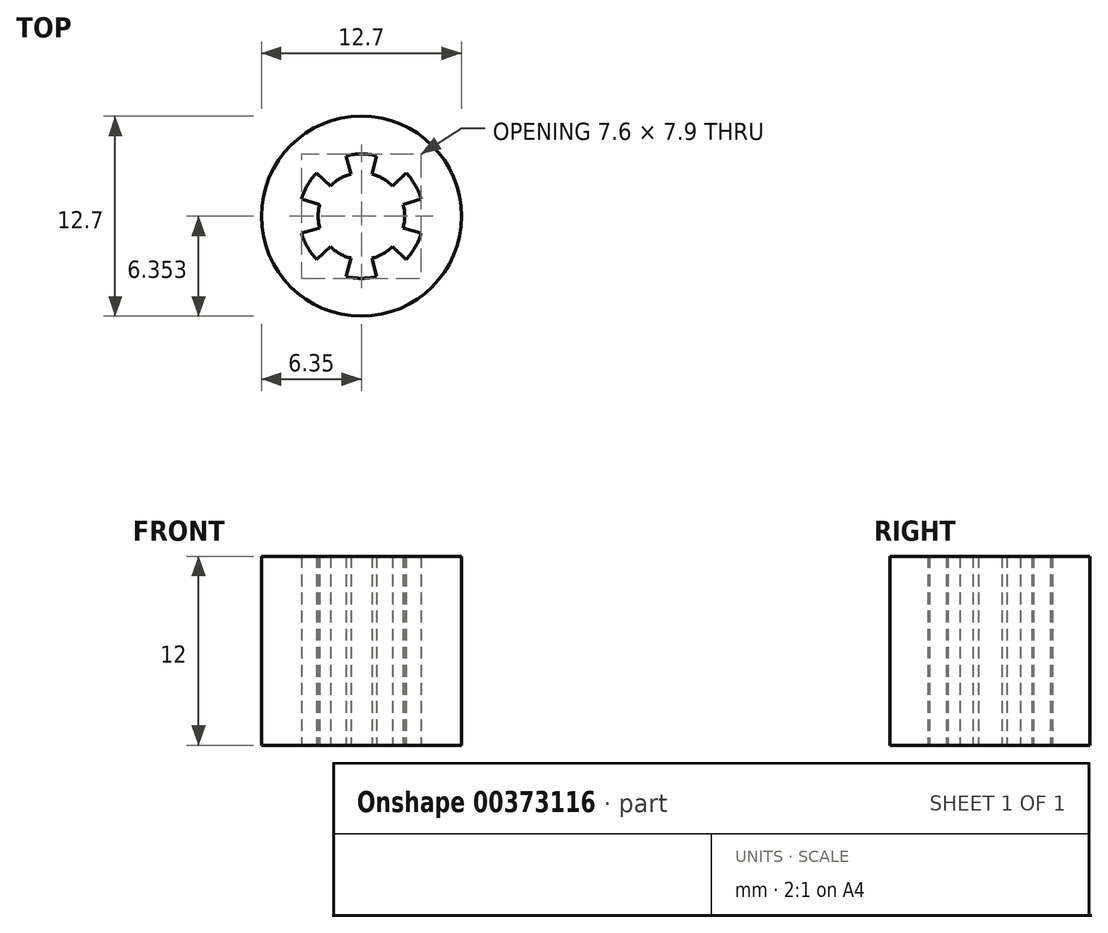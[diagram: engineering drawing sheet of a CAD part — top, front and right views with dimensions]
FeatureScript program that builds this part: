
annotation { "Feature Type Name" : "Feature", "Feature Type Description" : "" }
export const myFeature = defineFeature(function(context is Context, id is Id, definition is map)
    precondition{}
    {
        {
            var Q0;
            Q0=qCreatedBy(makeId("Top.planeOp"),FACE);
            var sketch = newSketch(context, id + "F0", { "sketchPlane" : qUnion([Q0])});
            skCircle(sketch, "E0.0", {"center": v(0, 0.1) * mm, "radius": 6.35 * mm});
            skArc(sketch, "E1", {"start": v(-2.65, 0.85) * mm, "mid": v(-2.75, 0.1) * mm, "end": v(-2.65, -0.65) * mm});
            skArc(sketch, "E2.0", {"start": v(-2.83, 2.86) * mm, "mid": v(-3.42, 2.08) * mm, "end": v(-3.8, 1.18) * mm});
            skLineSegment(sketch, "E3", {"start": v(0, 0.1) * mm, "end": v(0, 6.45) * mm, "construction": true});
            skLineSegment(sketch, "E4", {"start": v(-0.67, 2.77) * mm, "end": v(-0.97, 3.93) * mm});
            skLineSegment(sketch, "E5", {"start": v(-0.67, 2.77) * mm, "end": v(-2.33, 2.35) * mm, "construction": true});
            skLineSegment(sketch, "E6.MirrorCS", {"start": v(0.67, 2.77) * mm, "end": v(0.97, 3.93) * mm});
            skLineSegment(sketch, "E7.1.0", {"start": v(-1.97, 2.02) * mm, "end": v(-2.83, 2.86) * mm});
            skLineSegment(sketch, "E7.1.1", {"start": v(-2.65, 0.85) * mm, "end": v(-3.8, 1.18) * mm});
            skLineSegment(sketch, "E7.2.0", {"start": v(-2.65, -0.65) * mm, "end": v(-3.8, -0.97) * mm});
            skLineSegment(sketch, "E7.2.1", {"start": v(-1.97, -1.81) * mm, "end": v(-2.83, -2.65) * mm});
            skLineSegment(sketch, "E7.3.0", {"start": v(-0.67, -2.56) * mm, "end": v(-0.97, -3.73) * mm});
            skLineSegment(sketch, "E7.3.1", {"start": v(0.67, -2.56) * mm, "end": v(0.97, -3.73) * mm});
            skLineSegment(sketch, "E7.4.0", {"start": v(1.97, -1.81) * mm, "end": v(2.83, -2.65) * mm});
            skLineSegment(sketch, "E7.4.1", {"start": v(2.65, -0.65) * mm, "end": v(3.8, -0.97) * mm});
            skLineSegment(sketch, "E7.5.0", {"start": v(2.65, 0.85) * mm, "end": v(3.8, 1.18) * mm});
            skLineSegment(sketch, "E7.5.1", {"start": v(1.97, 2.02) * mm, "end": v(2.83, 2.86) * mm});
            skArc(sketch, "E8.trimOffspring", {"start": v(-1.97, -1.81) * mm, "mid": v(-1.38, -2.28) * mm, "end": v(-0.67, -2.56) * mm});
            skArc(sketch, "E9.trimOffspring", {"start": v(0.67, -2.56) * mm, "mid": v(1.37, -2.28) * mm, "end": v(1.97, -1.81) * mm});
            skArc(sketch, "E10.trimOffspring", {"start": v(2.65, -0.65) * mm, "mid": v(2.75, 0.1) * mm, "end": v(2.65, 0.85) * mm});
            skArc(sketch, "E11.trimOffspring", {"start": v(1.97, 2.02) * mm, "mid": v(1.37, 2.48) * mm, "end": v(0.67, 2.77) * mm});
            skArc(sketch, "E12.trimOffspring", {"start": v(-0.67, 2.77) * mm, "mid": v(-1.37, 2.48) * mm, "end": v(-1.97, 2.02) * mm});
            skArc(sketch, "E13.trimOffspring", {"start": v(-3.8, -0.97) * mm, "mid": v(-3.42, -1.87) * mm, "end": v(-2.83, -2.65) * mm});
            skArc(sketch, "E14.trimOffspring", {"start": v(-0.97, -3.73) * mm, "mid": v(0, -3.85) * mm, "end": v(0.97, -3.73) * mm});
            skArc(sketch, "E15.trimOffspring", {"start": v(2.83, -2.65) * mm, "mid": v(3.42, -1.87) * mm, "end": v(3.8, -0.97) * mm});
            skArc(sketch, "E16.trimOffspring", {"start": v(3.8, 1.18) * mm, "mid": v(3.42, 2.08) * mm, "end": v(2.83, 2.86) * mm});
            skArc(sketch, "E17.trimOffspring", {"start": v(0.97, 3.93) * mm, "mid": v(0, 4.05) * mm, "end": v(-0.97, 3.93) * mm});
            skSolve(sketch);
        }
        {
            var Q0;
            Q0 = qSketchRegion(id + "F0", true);
            extrude(context, id + "F1", {"entities" : qUnion([Q0]), "depth" : 12 * mm});
        }
    });
